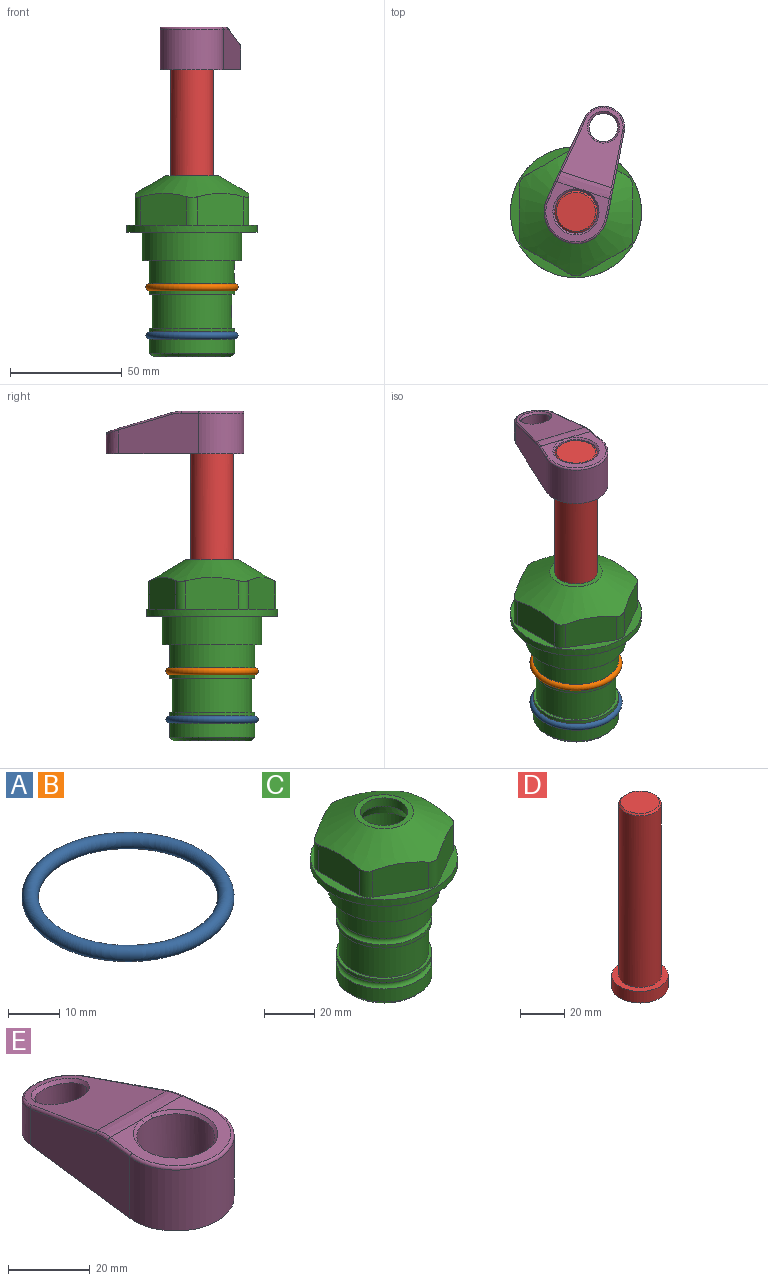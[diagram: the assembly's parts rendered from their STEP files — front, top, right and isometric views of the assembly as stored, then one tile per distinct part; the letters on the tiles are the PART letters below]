
ASSEMBLY  parts=5 mates=4
PART A: 1 faces, bbox 44.7x44.7x3.2 mm
  f0: torus R=19.05mm, axis (0,0,1), area 1193.9mm2
PART B: same geometry as A
PART C: 36 faces, bbox 58.7x58.7x81 mm
  f0: cylinder r=17.78mm len=35.56mm, axis (0,0,1), area 1670.8mm2, adj f23,f24,f31
  f1: cylinder r=19.05mm len=38.1mm, axis (0,0,1), area 1191.9mm2, adj f26,f27,f30
  f2: plane 58.66x58.66mm, normal (0,0,-1), area 1150.6mm2, adj f3,f28
  f3: cylinder r=29.33mm len=58.66mm, axis (0,0,-1), area 585.1mm2, adj f2,f4
  f4: plane 58.66x58.66mm, normal (0,0,1), area 475.9mm2, adj f3,f5,f6,f7,f8,f9,f10,f11
  f5: plane 20.32x14.34mm, normal (-0.5,0.87,0), area 324.4mm2, adj f4,f15,f16,f17
  f6: plane 20.32x14.34mm, normal (0.5,0.87,0), area 324.4mm2, adj f4,f14,f15,f17
  f7: plane 23.48x14.34mm, normal (1,0,0), area 324.4mm2, adj f4,f13,f14,f17
  f8: plane 20.32x14.34mm, normal (0.5,-0.87,0), area 324.4mm2, adj f4,f12,f13,f17
  f9: plane 20.32x14.34mm, normal (-0.5,-0.87,0), area 324.4mm2, adj f4,f11,f12,f17
  f10: plane 23.48x14.34mm, normal (-1,0,0), area 324.4mm2, adj f4,f11,f16,f17
  f11: cylinder r=5.08mm len=12.85mm, axis (0,0,-1), area 67.2mm2, adj f4,f9,f10,f17
  f12: cylinder r=5.08mm len=12.85mm, axis (0,0,-1), area 67.2mm2, adj f4,f8,f9,f17
  f13: cylinder r=5.08mm len=12.85mm, axis (0,0,-1), area 67.2mm2, adj f4,f7,f8,f17
  f14: cylinder r=5.08mm len=12.85mm, axis (0,0,-1), area 67.2mm2, adj f4,f6,f7,f17
  f15: cylinder r=5.08mm len=12.85mm, axis (0,0,-1), area 67.2mm2, adj f4,f5,f6,f17
  f16: cylinder r=5.08mm len=12.85mm, axis (0,0,-1), area 67.2mm2, adj f4,f5,f10,f17
  f17: cone r=11.73mm half-angle=60deg, axis (0,0,-1), area 2071.8mm2, adj f5,f6,f7,f8,f9,f10,f11,f12
  f18: plane 23.46x23.46mm, normal (0,0,1), area 147.4mm2, adj f17,f35
  f19: plane 34.93x34.93mm, normal (0,0,-1), area 958mm2, adj f29
  f20: cylinder r=19.05mm len=38.1mm, axis (0,0,1), area 760.1mm2, adj f21,f29
  f21: torus R=19.05mm, axis (0,0,1), area 565.3mm2, adj f20,f22
  f22: cylinder r=19.05mm len=38.1mm, axis (0,0,1), area 190mm2, adj f21,f23
  f23: plane 38.1x38.1mm, normal (0,0,1), area 146.9mm2, adj f0,f22
  f24: plane 38.1x38.1mm, normal (0,0,-1), area 146.9mm2, adj f0,f25
  f25: cylinder r=19.05mm len=38.1mm, axis (0,0,1), area 190mm2, adj f24,f26
  f26: torus R=19.05mm, axis (0,0,1), area 565.3mm2, adj f1,f25
  f27: plane 44.45x44.45mm, normal (0,0,-1), area 411.7mm2, adj f1,f28
  f28: cylinder r=22.23mm len=44.45mm, axis (0,0,1), area 1773.5mm2, adj f2,f27
  f29: cone r=19.05mm half-angle=45deg, axis (0,0,1), area 257.5mm2, adj f19,f20
  f30: cylinder r=3.17mm len=6.75mm, axis (-1,0,0), area 128mm2, adj f1,f33
  f31: cylinder r=3.17mm len=6.35mm, axis (-1,0,0), area 102.5mm2, adj f0,f33
  f32: plane 25.4x25.4mm, normal (0,0,1), area 506.7mm2, adj f33
  f33: cylinder r=12.7mm len=66.42mm, axis (0,0,-1), area 5236.2mm2, adj f30,f31,f32,f34
  f34: cone r=9.53mm half-angle=30deg, axis (0,0,-1), area 443.4mm2, adj f33,f35
  f35: cylinder r=9.53mm len=19.05mm, axis (0,0,-1), area 240.9mm2, adj f18,f34
PART D: 6 faces, bbox 25.4x25.4x101.6 mm
  f0: plane 17.46x17.46mm, normal (0,0,1), area 239.5mm2, adj f5
  f1: plane 25.4x25.4mm, normal (0,0,-1), area 506.7mm2, adj f2
  f2: cylinder r=12.7mm len=25.4mm, axis (0,0,1), area 506.7mm2, adj f1,f3
  f3: plane 25.4x25.4mm, normal (0,0,1), area 221.7mm2, adj f2,f4
  f4: cylinder r=9.53mm len=94.46mm, axis (0,0,1), area 5653mm2, adj f3,f5
  f5: cone r=8.73mm half-angle=45deg, axis (0,0,-1), area 64.4mm2, adj f0,f4
PART E: 31 faces, bbox 31.7x65.5x19.8 mm
  f0: plane 39.12x18.26mm, normal (0.99,0.12,0), area 612.2mm2, adj f1,f4,f7,f11,f13,f15
  f1: cylinder r=9.53mm len=18.91mm, axis (0,0,-1), area 296.1mm2, adj f0,f2,f7,f17
  f2: plane 39.12x18.26mm, normal (-0.99,0.12,0), area 612.2mm2, adj f1,f4,f7,f12,f14,f16
  f3: cylinder r=6.35mm len=12.7mm, axis (0,0,-1), area 362.4mm2, adj f7,f18
  f4: cylinder r=14.29mm len=28.58mm, axis (0,0,-1), area 882.2mm2, adj f0,f2,f7,f10
  f5: cylinder r=9.53mm len=19.05mm, axis (0,0,-1), area 1092.6mm2, adj f7,f19,f20
  f6: plane 26.99x23.69mm, normal (0,0,1), area 216.2mm2, adj f9,f10,f11,f12,f19
  f7: plane 63.5x28.58mm, normal (0,0,-1), area 661.8mm2, adj f0,f1,f2,f3,f4,f5,f22,f23
  f8: plane 33.52x23.6mm, normal (0,0.26,0.97), area 486mm2, adj f9,f15,f16,f17,f18
  f9: cylinder r=19.05mm len=24.72mm, axis (1,0,0), area 120.4mm2, adj f6,f8,f13,f14,f20
  f10: torus R=13.49mm, axis (0,0,1), area 59mm2, adj f4,f6,f11,f12
  f11: cylinder r=0.79mm len=8.67mm, axis (0.12,-0.99,0), area 10.8mm2, adj f0,f6,f10,f13
  f12: cylinder r=0.79mm len=8.67mm, axis (0.12,0.99,0), area 10.8mm2, adj f2,f6,f10,f14
  f13: bspline ~4.95x1.42mm, area 6.1mm2, adj f0,f9,f11,f15
  f14: bspline ~4.95x1.42mm, area 6.1mm2, adj f2,f9,f12,f16
  f15: cylinder r=0.79mm len=25.95mm, axis (0.12,-0.96,0.26), area 32.9mm2, adj f0,f8,f13,f17
  f16: cylinder r=0.79mm len=25.95mm, axis (0.12,0.96,-0.26), area 32.9mm2, adj f2,f8,f14,f17
  f17: bspline ~18.91x8.38mm, area 30mm2, adj f1,f8,f15,f16
  f18: bspline ~14.29x14.29mm, area 48.3mm2, adj f3,f8
  f19: cone r=9.53mm half-angle=45deg, axis (0,0,1), area 66.5mm2, adj f5,f6,f20
  f20: bspline ~3.22x0.96mm, area 3.5mm2, adj f5,f9,f19
  f21: plane 2.75x2.72mm, normal (0,0,-1), area 2.9mm2, adj f23,f25,f28
  f22: plane 23.05x15.88mm, normal (-0.99,-0.12,0), area 323.6mm2, adj f7,f25,f26,f27,f28,f29
  f23: plane 23.05x15.88mm, normal (0.99,-0.12,0), area 323.6mm2, adj f7,f21,f25,f27,f28,f30
  f24: cylinder r=9.53mm len=10.69mm, axis (0,0,-1), area 114.7mm2, adj f7,f27,f29,f30
  f25: cylinder r=12.7mm len=20.59mm, axis (0,0,-1), area 381.1mm2, adj f7,f21,f22,f23,f26,f28
  f26: plane 2.75x2.72mm, normal (0,0,-1), area 2.9mm2, adj f22,f25,f28
  f27: plane 19.72x18.37mm, normal (0,-0.26,-0.97), area 291.8mm2, adj f22,f23,f24,f28,f29,f30
  f28: cylinder r=15.88mm len=19.92mm, axis (1,0,0), area 54.8mm2, adj f21,f22,f23,f25,f26,f27
  f29: cylinder r=1.59mm len=11mm, axis (0,0,-1), area 34.7mm2, adj f7,f22,f24,f27
  f30: cylinder r=1.59mm len=11mm, axis (0,0,-1), area 34.7mm2, adj f7,f23,f24,f27
PLACE A t=(0,0,-21.59)mm
PLACE B at identity
PLACE C at identity fixed
PLACE D rot(axis=(0,0,-1),18deg) t=(0,0,27.55)mm
PLACE E rot(axis=(0,0,-1),18deg) t=(0,0,28.35)mm
MATE fastened E.f4 <-> D.f2  axis (0,0,-1) through (0,0,91.05)mm
MATE cylindrical C.f0 <-> D.f2  axis (0,0,1) through (0,0,-50.55)mm
MATE fastened A.f0 <-> C.f0  axis (0,0,1) through (0,0,-46.1)mm
MATE fastened B.f0 <-> C.f0  axis (0,0,1) through (0,0,-24.51)mm
